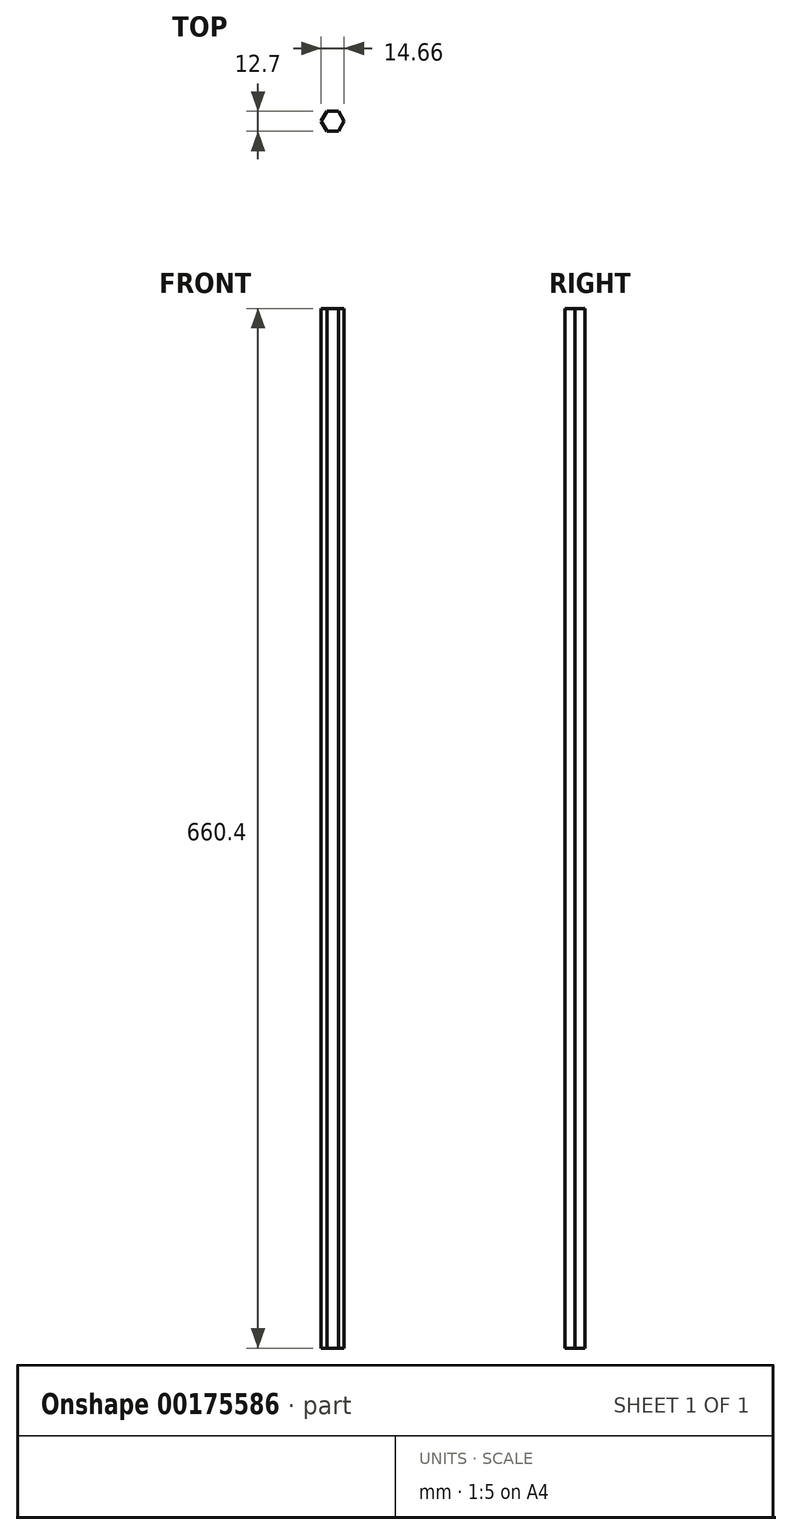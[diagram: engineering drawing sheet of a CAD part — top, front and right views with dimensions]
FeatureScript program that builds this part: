
annotation { "Feature Type Name" : "Feature", "Feature Type Description" : "" }
export const myFeature = defineFeature(function(context is Context, id is Id, definition is map)
    precondition{}
    {
        {
            var Q0;
            Q0=qCreatedBy(makeId("Top.planeOp"),FACE);
            var sketch = newSketch(context, id + "F0", { "sketchPlane" : qUnion([Q0])});
            skCircle(sketch, "E0.cCircle", {"center": v(0, 0) * mm, "radius": 6.35 * mm, "construction": true});
            skLineSegment(sketch, "E0.0", {"start": v(-3.67, 6.35) * mm, "end": v(3.67, 6.35) * mm});
            skLineSegment(sketch, "E0.1", {"start": v(3.67, 6.35) * mm, "end": v(7.33, 0) * mm});
            skLineSegment(sketch, "E0.2", {"start": v(7.33, 0) * mm, "end": v(3.67, -6.35) * mm});
            skLineSegment(sketch, "E0.3", {"start": v(3.67, -6.35) * mm, "end": v(-3.67, -6.35) * mm});
            skLineSegment(sketch, "E0.4", {"start": v(-3.67, -6.35) * mm, "end": v(-7.33, 0) * mm});
            skLineSegment(sketch, "E0.5", {"start": v(-7.33, 0) * mm, "end": v(-3.67, 6.35) * mm});
            skPoint(sketch, "E0.0.midPoint", {"position": v(0, 6.35) * mm});
            skSolve(sketch);
        }
        {
            var Q0;
            Q0=makeQuery(id+"F0.imprint","IMPRINT",FACE,{"disambiguationData":[TD([[makeQuery(id+"F0.imprint","IMPRINT",EDGE,{"derivedFrom":sQuery(id+"F0.wireOp",EDGE,"E0.0")}),-1.0]])]});
            extrude(context, id + "F1", {"entities" : qUnion([Q0]), "depth" : 660.4 * mm});
        }
    });
